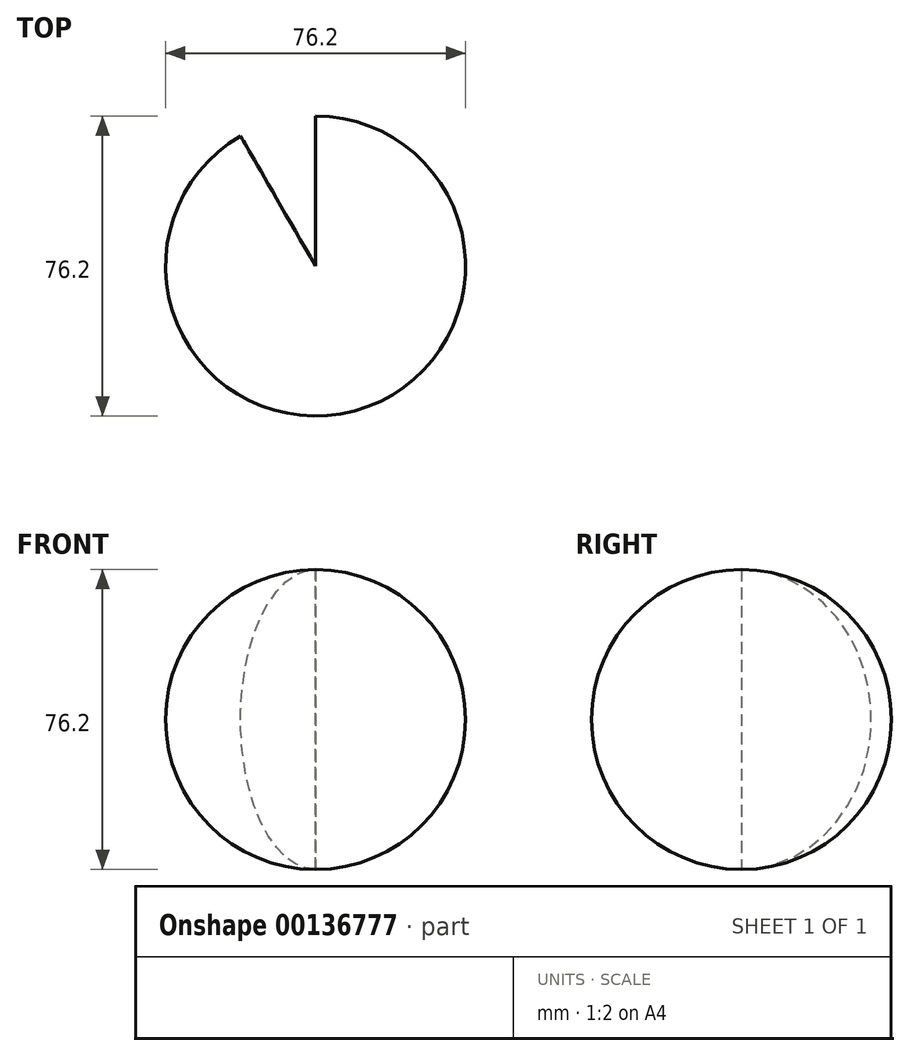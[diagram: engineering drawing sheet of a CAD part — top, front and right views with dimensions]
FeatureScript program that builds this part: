
annotation { "Feature Type Name" : "Feature", "Feature Type Description" : "" }
export const myFeature = defineFeature(function(context is Context, id is Id, definition is map)
    precondition{}
    {
        {
            var Q0;
            Q0=qCreatedBy(makeId("Right.planeOp"),FACE);
            var sketch = newSketch(context, id + "F0", { "sketchPlane" : qUnion([Q0])});
            skArc(sketch, "E0", {"start": v(0, -38.1) * mm, "mid": v(38.1, 0) * mm, "end": v(0, 38.1) * mm});
            skLineSegment(sketch, "E1", {"start": v(0, 38.1) * mm, "end": v(0, -38.1) * mm});
            skSolve(sketch);
        }
        {
            var Q0;
            Q0 = qSketchRegion(id + "F0", true);
            var Q1;
            Q1=sQuery(id+"F0.wireOp",EDGE,"E1");
            revolve(context, id + "F1", {"entities" : qUnion([Q0]), "axis" : qUnion([Q1]), "revolveType" : RevolveType.ONE_DIRECTION, "angle" : 330 * degree});
        }
    });
